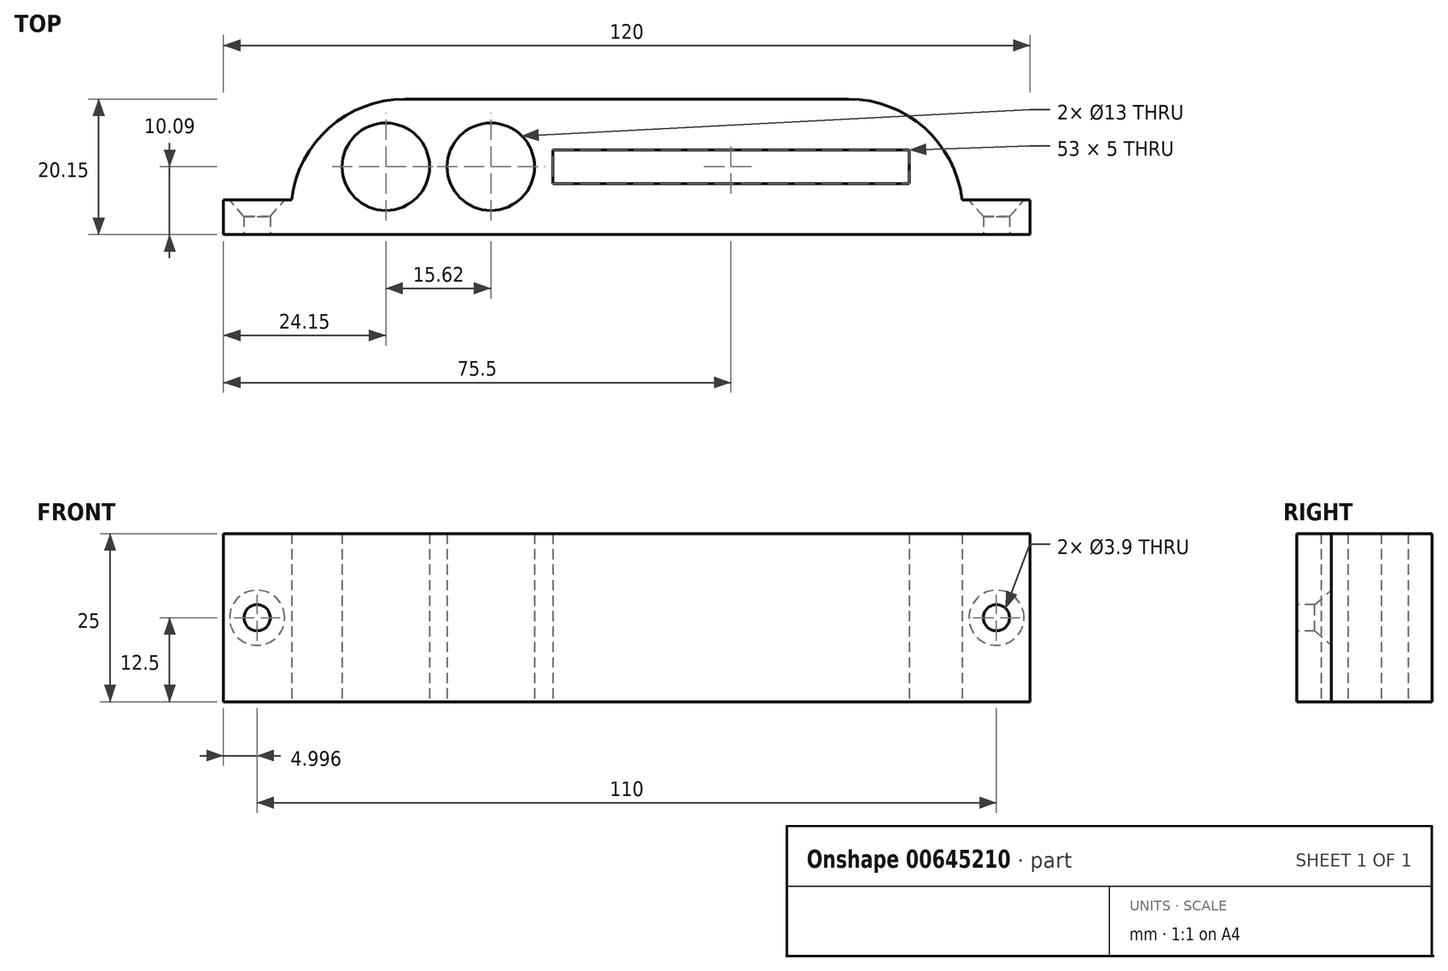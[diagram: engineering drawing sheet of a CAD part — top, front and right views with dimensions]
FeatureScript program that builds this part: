
annotation { "Feature Type Name" : "Feature", "Feature Type Description" : "" }
export const myFeature = defineFeature(function(context is Context, id is Id, definition is map)
    precondition{}
    {
        {
            var Q0;
            Q0=qCreatedBy(makeId("Top.planeOp"),FACE);
            var sketch = newSketch(context, id + "F0", { "sketchPlane" : qUnion([Q0])});
            skLineSegment(sketch, "E0.bottom", {"start": v(52.54, 0) * mm, "end": v(-67.46, 0) * mm});
            skLineSegment(sketch, "E0.top", {"start": v(25.54, 20.15) * mm, "end": v(-40.46, 20.15) * mm});
            skLineSegment(sketch, "E0.left", {"start": v(52.54, 0) * mm, "end": v(52.54, 3.15) * mm});
            skLineSegment(sketch, "E0.right", {"start": v(-67.46, 0) * mm, "end": v(-67.46, 3.15) * mm});
            skPoint(sketch, "E1", {"position": v(-40.46, 20.15) * mm});
            skArc(sketch, "E2", {"start": v(-40.46, 20.15) * mm, "mid": v(-51.76, 15.86) * mm, "end": v(-57.35, 5.15) * mm});
            skLineSegment(sketch, "E3", {"start": v(-7.46, 0) * mm, "end": v(-7.46, 20) * mm, "construction": true});
            skArc(sketch, "E4.MirrorCS", {"start": v(25.54, 20.15) * mm, "mid": v(36.83, 15.86) * mm, "end": v(42.42, 5.15) * mm});
            skLineSegment(sketch, "E5.bottom", {"start": v(34.54, 7.59) * mm, "end": v(-18.46, 7.59) * mm});
            skLineSegment(sketch, "E5.top", {"start": v(34.54, 12.59) * mm, "end": v(-18.46, 12.59) * mm});
            skLineSegment(sketch, "E5.left", {"start": v(34.54, 7.59) * mm, "end": v(34.54, 12.59) * mm});
            skLineSegment(sketch, "E5.right", {"start": v(-18.46, 7.59) * mm, "end": v(-18.46, 12.59) * mm});
            skCircle(sketch, "E6", {"center": v(-27.7, 10.09) * mm, "radius": 6.5 * mm});
            skCircle(sketch, "E7", {"center": v(-43.31, 10.09) * mm, "radius": 6.5 * mm});
            skLineSegment(sketch, "E8", {"start": v(-43.31, 10.09) * mm, "end": v(-18.46, 10.09) * mm, "construction": true});
            skLineSegment(sketch, "E9", {"start": v(-67.46, 3.15) * mm, "end": v(-67.46, 5.15) * mm});
            skLineSegment(sketch, "E10", {"start": v(-67.46, 5.15) * mm, "end": v(-57.46, 5.15) * mm});
            skLineSegment(sketch, "E11", {"start": v(52.54, 3.15) * mm, "end": v(52.54, 5.15) * mm});
            skLineSegment(sketch, "E12", {"start": v(52.54, 5.15) * mm, "end": v(42.42, 5.15) * mm});
            skLineSegment(sketch, "E13", {"start": v(-57.46, 5.15) * mm, "end": v(-57.35, 5.15) * mm});
            skSolve(sketch);
        }
        {
            var Q0;
            Q0=makeQuery(id+"F0.imprint","IMPRINT",FACE,{"disambiguationData":[TD([[makeQuery(id+"F0.imprint","IMPRINT",EDGE,{"derivedFrom":sQuery(id+"F0.wireOp",EDGE,"E0.top")}),1.0]])]});
            var Q1;
            Q1=makeQuery(id+"F0.imprint","IMPRINT",FACE,{"disambiguationData":[TD([[makeQuery(id+"F0.imprint","IMPRINT",EDGE,{"derivedFrom":sQuery(id+"F0.wireOp",EDGE,"E0.bottom")}),-1.0]])]});
            extrude(context, id + "F1", {"entities" : qUnion([Q0, Q1]), "depth" : 25 * mm, "offsetDistance" : 25 * mm});
        }
        {
            var Q0;
            Q0=makeQuery(id+"F1.opExtrude","SWEPT_FACE",FACE,{"disambiguationData":[OSD([sQuery(id+"F0.wireOp",EDGE,"E10"),sQuery(id+"F0.wireOp",EDGE,"E13")])]});
            var sketch = newSketch(context, id + "F2", { "sketchPlane" : qUnion([Q0])});
            skLineSegment(sketch, "E14.0", {"start": v(67.46, 20) * mm, "end": v(67.46, 5) * mm});
            skLineSegment(sketch, "E14.1", {"start": v(57.35, 25) * mm, "end": v(57.35, 0) * mm});
            skLineSegment(sketch, "E14.2", {"start": v(62.46, 0) * mm, "end": v(57.35, 0) * mm});
            skLineSegment(sketch, "E14.3", {"start": v(62.46, 25) * mm, "end": v(57.35, 25) * mm});
            skLineSegment(sketch, "E15", {"start": v(67.46, 12.5) * mm, "end": v(57.35, 12.5) * mm, "construction": true});
            skLineSegment(sketch, "E16", {"start": v(62.46, 0) * mm, "end": v(62.46, 25) * mm, "construction": true});
            skPoint(sketch, "E17", {"position": v(62.46, 12.5) * mm});
            skLineSegment(sketch, "E18.0", {"start": v(-42.42, 25) * mm, "end": v(-42.42, 0) * mm});
            skLineSegment(sketch, "E18.1", {"start": v(-52.54, 20) * mm, "end": v(-52.54, 5) * mm});
            skLineSegment(sketch, "E18.2", {"start": v(-47.54, 0) * mm, "end": v(-42.42, 0) * mm});
            skLineSegment(sketch, "E18.3", {"start": v(-47.54, 25) * mm, "end": v(-42.42, 25) * mm});
            skLineSegment(sketch, "E19", {"start": v(-52.54, 12.5) * mm, "end": v(-42.42, 12.5) * mm, "construction": true});
            skLineSegment(sketch, "E20", {"start": v(-47.54, 0) * mm, "end": v(-47.54, 25) * mm, "construction": true});
            skPoint(sketch, "E21", {"position": v(-47.54, 12.5) * mm});
            skSolve(sketch);
        }
        {
            var Q0;
            Q0=sQuery(id+"F2.wireOp",VERTEX,"E17");
            var Q1;
            Q1=sQuery(id+"F2.wireOp",VERTEX,"E21");
            var Q2;
            Q2=makeQuery(id+"F1.opExtrude","SWEPT_BODY",BODY,{"disambiguationData":[OSD([sQuery(id+"F0.wireOp",EDGE,"E0.bottom"),sQuery(id+"F0.wireOp",EDGE,"E0.top"),sQuery(id+"F0.wireOp",EDGE,"E0.left"),sQuery(id+"F0.wireOp",EDGE,"E0.right"),sQuery(id+"F0.wireOp",EDGE,"E2"),sQuery(id+"F0.wireOp",EDGE,"E4.MirrorCS"),sQuery(id+"F0.wireOp",EDGE,"E5.bottom"),sQuery(id+"F0.wireOp",EDGE,"E5.top"),sQuery(id+"F0.wireOp",EDGE,"E5.left"),sQuery(id+"F0.wireOp",EDGE,"E5.right"),sQuery(id+"F0.wireOp",EDGE,"E6"),sQuery(id+"F0.wireOp",EDGE,"E7"),sQuery(id+"F0.wireOp",EDGE,"E9"),sQuery(id+"F0.wireOp",EDGE,"E10"),sQuery(id+"F0.wireOp",EDGE,"E11"),sQuery(id+"F0.wireOp",EDGE,"E12"),sQuery(id+"F0.wireOp",EDGE,"E13")])]});
            hole(context, id + "F3", {"style" : HoleStyle.C_SINK, "endStyle" : HoleEndStyle.THROUGH, "holeDiameter" : 3.9 * mm, "cSinkDiameter" : 8.2 * mm, "cSinkAngle" : 82 * degree, "majorDiameter" : 5 * mm, "isTappedThrough" : true, "tappedDepth" : 12 * mm, "tapClearance" : 3, "locations" : qUnion([Q0, Q1]), "scope" : qUnion([Q2]), "startStyle" : HoleStartStyle.SKETCH});
        }
    });
